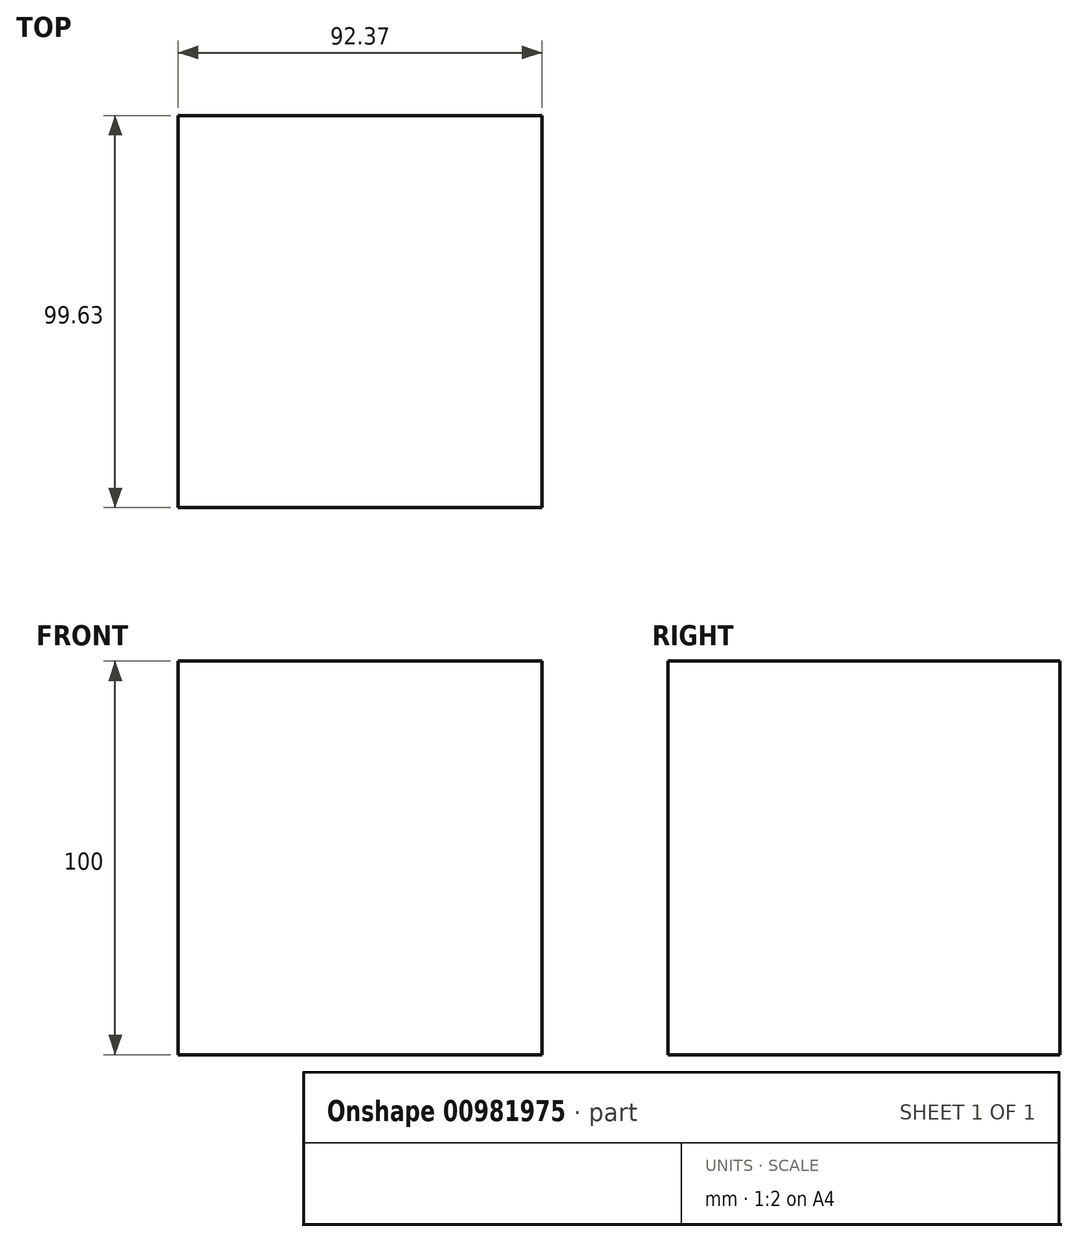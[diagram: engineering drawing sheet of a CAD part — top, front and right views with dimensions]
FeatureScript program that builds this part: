
annotation { "Feature Type Name" : "Feature", "Feature Type Description" : "" }
export const myFeature = defineFeature(function(context is Context, id is Id, definition is map)
    precondition{}
    {
        {
            var Q0;
            Q0=qCreatedBy(makeId("Top.planeOp"),FACE);
            var sketch = newSketch(context, id + "F0", { "sketchPlane" : qUnion([Q0])});
            skLineSegment(sketch, "E0.bottom", {"start": v(-69.72, -58.23) * mm, "end": v(22.65, -58.23) * mm});
            skLineSegment(sketch, "E0.top", {"start": v(-69.72, 41.4) * mm, "end": v(22.65, 41.4) * mm});
            skLineSegment(sketch, "E0.left", {"start": v(-69.72, -58.23) * mm, "end": v(-69.72, 41.4) * mm});
            skLineSegment(sketch, "E0.right", {"start": v(22.65, -58.23) * mm, "end": v(22.65, 41.4) * mm});
            skSolve(sketch);
        }
        {
            var Q0;
            Q0 = qSketchRegion(id + "F0", true);
            extrude(context, id + "F1", {"entities" : qUnion([Q0]), "depth" : 100 * mm, "offsetDistance" : 25.4 * mm});
        }
    });
